# Revit family: 50_series_non_automatic
name_source: partatom
category: Mechanical Equipment
revit_build: Autodesk Revit 2013 (Build: 20120221_2030(x64)
units: mm (PartAtom-declared; Revit-internal decimal feet)

## types (8) — shared parameters
Assembly Code = D2010900
Cooling = Oil Filled
Cord Length (Auto/Non-Auto) = 108" (Automatic), 180" (Non-Automatic)
Cord Type = UL listed, 3-wire cord and plug
Default Elevation = 7 7/8"
Description = Submersible Pump for Dewatering or Effluent (Septic Tank Systems)
Discharge Diameter = 1 1/2" NPT
Discharge Height = 3 3/32"
Discharge Radius = 3/4"
Height = 10 1/16"
Hertz = 60
Impeller Type = Non-clogging vortex impeller
Installation Type = Floor Mounted
Insulation = Class B
Lead Wires Insulation = Class B
Length = 7 7/8"
Lower Bearing = Sleeve Bearing
Manufacturer = Zoeller
Masterformat Number = 33 36 16
Masterformat Title = Utility Septic Tank Effluent Pumps
Max Flow Rate @ 5’ Hd = 43 gpm
Max. Water Temp. = 130 °F
Maximum Head = 19 1/4 ft
Motor = 3/10 HP
Motor Thermal Shutoff (Single Phase Only) = Thermal Overload Sensors With Automatic Reset.
Motor Type = Submersible
O-Rings and Cover Gasket = Neoprene
Omniclass Table 23 Code = 23.60.30.21
Omniclass Table 23 Title = Pumps
Operation = Non-automatic
Phase = 1
Price = Prices may vary. Please consult Manufacturer Representative for most up-to-date price list.
Product Page URL = http://www.zoellerpumps.com
RPM = 1550
Shaft Seal = Carbon/Ceramic
Solid Handling = 1/2" Spherical Solids
Type = Shaded Pole Motor
Type Comments = Automatic or Non-Automatic available
URL = http://www.zoellerengprod.com
Upper Bearing = Sleeve Bearing
Warranty Information = 36 Months (Limited)
Waste Connection = Yes
Width = 10 3/32"

## per-type parameters (varying)
| type | Amps | Apparent Load | Impeller | Material | Model | Voltage |
| 53 - 115 volt | 10 A | 1116 VA | Engineered Thermoplastic | Cast Iron-Zoeller-Powder Coated Epoxy | 53 | 115 V |
| 55 - 115 volt | 10 A | 1116 VA | Engineered Thermoplastic | Cast Iron-Zoeller-Powder Coated Epoxy | 55 | 115 V |
| 57 - 115 volt | 10 A | 1116 VA | Cast Iron | Cast Iron-Zoeller-Powder Coated Epoxy | 57 | 115 V |
| 59 - 115 volt | 10 A | 1116 VA | Bronze | Bronze | 59 | 115 V |
| 53 - 230 volt | 5 A | 1104 VA | Engineered Thermoplastic | Cast Iron-Zoeller-Powder Coated Epoxy | 53 | 230 V |
| 55 - 230 volt | 5 A | 1104 VA | Engineered Thermoplastic | Cast Iron-Zoeller-Powder Coated Epoxy | 55 | 230 V |
| 57 - 230 volt | 5 A | 1104 VA | Cast Iron | Cast Iron-Zoeller-Powder Coated Epoxy | 57 | 230 V |
| 59 - 230 volt | 5 A | 1104 VA | Bronze | Bronze | 59 | 230 V |

## geometry (parser evidence)
native form markers: Blend x10
no freeform markers — native parametric forms only
